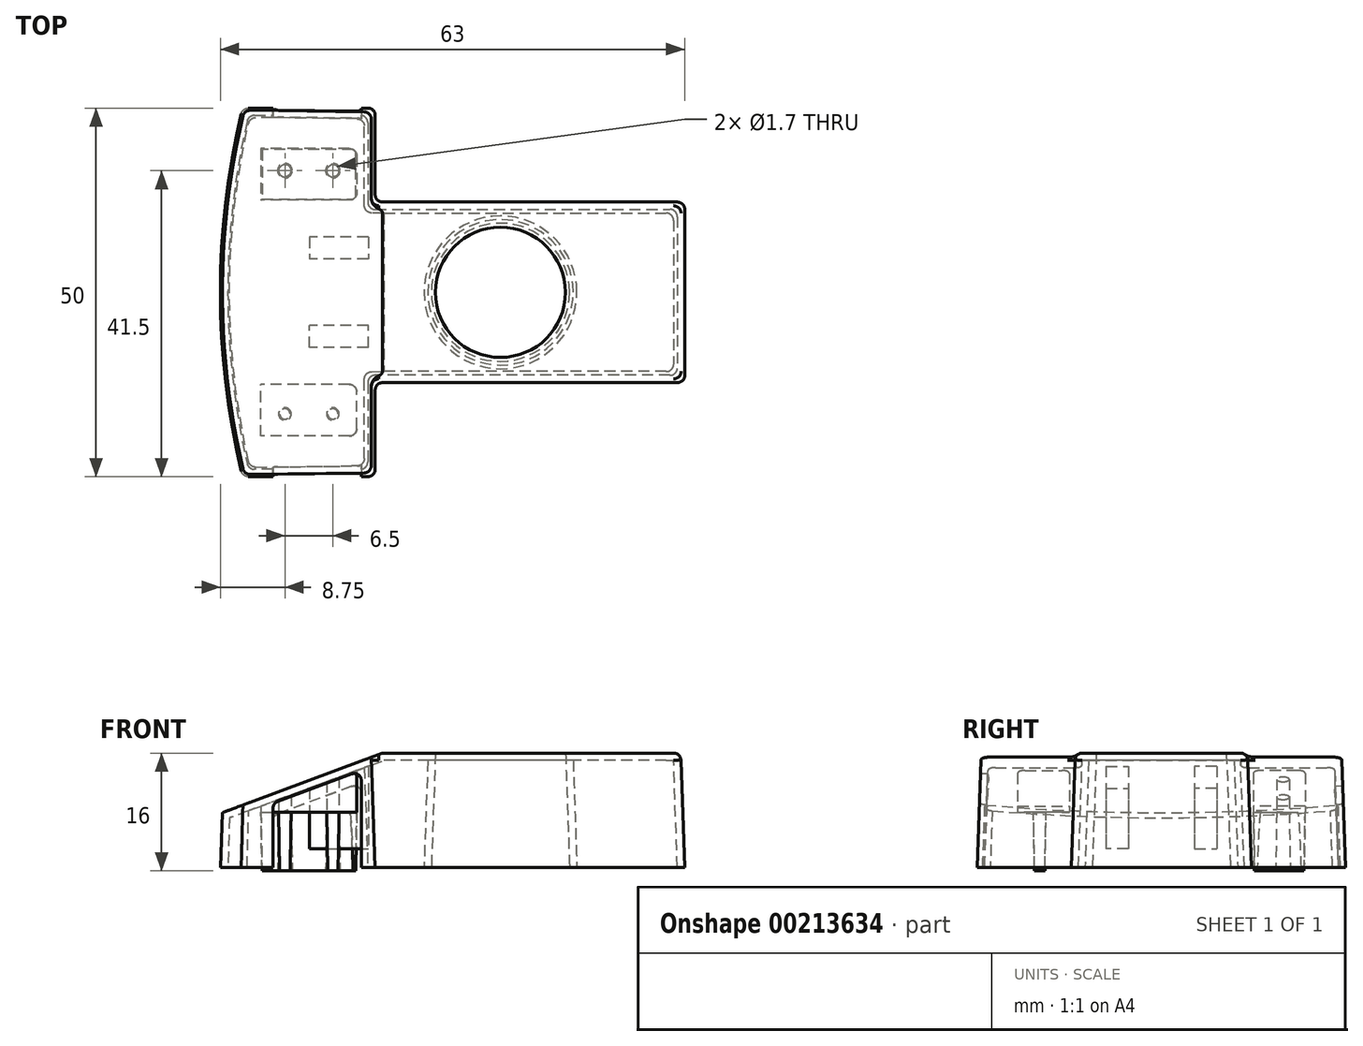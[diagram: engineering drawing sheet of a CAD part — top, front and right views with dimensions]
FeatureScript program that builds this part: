
annotation { "Feature Type Name" : "Feature", "Feature Type Description" : "" }
export const myFeature = defineFeature(function(context is Context, id is Id, definition is map)
    precondition{}
    {
        {
            var Q0;
            Q0=qCreatedBy(makeId("Top.planeOp"),FACE);
            var sketch = newSketch(context, id + "F0", { "sketchPlane" : qUnion([Q0])});
            skCircle(sketch, "E0", {"center": v(-4, 0) * mm, "radius": 9.37 * mm});
            skLineSegment(sketch, "E1.bottom", {"start": v(-21, -12.25) * mm, "end": v(21, -12.25) * mm});
            skLineSegment(sketch, "E1.top", {"start": v(-21, 12.25) * mm, "end": v(21, 12.25) * mm});
            skLineSegment(sketch, "E1.right", {"start": v(21, -12.25) * mm, "end": v(21, 12.25) * mm});
            skLineSegment(sketch, "E2.bottom", {"start": v(-21, -25) * mm, "end": v(-39, -25) * mm});
            skLineSegment(sketch, "E2.top", {"start": v(-21, 25) * mm, "end": v(-39, 25) * mm});
            skLineSegment(sketch, "E2.left", {"start": v(-21, -25) * mm, "end": v(-21, -12.25) * mm});
            skLineSegment(sketch, "E2.right", {"start": v(-39, -25) * mm, "end": v(-39, 25) * mm});
            skPoint(sketch, "E2.middle", {"position": v(-30, 0) * mm});
            skLineSegment(sketch, "E3.trimOffspring", {"start": v(-21, 12.25) * mm, "end": v(-21, 25) * mm});
            skLineSegment(sketch, "E4", {"start": v(-20, 12.25) * mm, "end": v(-20, -12.25) * mm});
            skPoint(sketch, "E5", {"position": v(-42, 0) * mm});
            skPoint(sketch, "E5.positionSnap0", {"position": v(-39, 0) * mm});
            skArc(sketch, "E6", {"start": v(-39, 25) * mm, "mid": v(-42, 0) * mm, "end": v(-39, -25) * mm});
            skSolve(sketch);
        }
        {
            var Q0;
            Q0=qSketchRegion(id+"F0",true);
            var Q1;
            Q1=makeQuery(id+"F0.imprint","IMPRINT",FACE,{"disambiguationData":[TD([[makeQuery(id+"F0.imprint","IMPRINT",EDGE,{"derivedFrom":sQuery(id+"F0.wireOp",EDGE,"E0")}),1.0]])]});
            extrude(context, id + "F1", {"entities" : qUnion([Q0, Q1]), "depth" : 15.5 * mm, "hasDraft" : true, "draftAngle" : 2 * degree, "draftPullDirection" : true});
        }
        {
            var Q0;
            Q0=makeQuery(id+"F0.imprint","IMPRINT",FACE,{"disambiguationData":[TD([[makeQuery(id+"F0.imprint","IMPRINT",EDGE,{"derivedFrom":sQuery(id+"F0.wireOp",EDGE,"E0")}),1.0]])]});
            var Q1;
            Q1=makeQuery(id+"F1.opExtrude","CAP_FACE",FACE,{"disambiguationData":[OSD([sQuery(id+"F0.wireOp",EDGE,"E1.bottom"),sQuery(id+"F0.wireOp",EDGE,"E1.top"),sQuery(id+"F0.wireOp",EDGE,"E1.right"),sQuery(id+"F0.wireOp",EDGE,"E2.bottom"),sQuery(id+"F0.wireOp",EDGE,"E2.top"),sQuery(id+"F0.wireOp",EDGE,"E2.left"),sQuery(id+"F0.wireOp",EDGE,"E3.trimOffspring"),sQuery(id+"F0.wireOp",EDGE,"E6")])],"isStart":false});
            extrude(context, id + "F2", {"entities" : qUnion([Q0]), "operationType" : NewBodyOperationType.REMOVE, "endBound" : BoundingType.UP_TO_SURFACE, "endBoundEntityFace" : qUnion([Q1]), "depth" : 25 * mm, "hasDraft" : true, "draftAngle" : 2 * degree, "draftPullDirection" : true});
        }
        {
            var Q0;
            Q0=qCreatedBy(makeId("Front.planeOp"),FACE);
            var Q1;
            Q1=makeQuery(id+"F1.opExtrude","CAP_EDGE",EDGE,{"disambiguationData":[OSD([sQuery(id+"F0.wireOp",EDGE,"E2.bottom")])],"isStart":true});
            cPlane(context, id + "F3", {"entities" : qUnion([Q0, Q1]), "cplaneType" : CPlaneType.LINE_ANGLE, "offset" : 25 * mm, "angle" : 0 * degree, "width" : 150 * mm, "height" : 150 * mm});
        }
        {
            var Q0;
            Q0=qCreatedBy(id+"F3.planeOp",FACE);
            var sketch = newSketch(context, id + "F4", { "sketchPlane" : qUnion([Q0])});
            skLineSegment(sketch, "E7", {"start": v(20, 15.5) * mm, "end": v(42, 15.5) * mm});
            skLineSegment(sketch, "E8", {"start": v(42, 15.5) * mm, "end": v(42, 7.32) * mm});
            skLineSegment(sketch, "E9", {"start": v(42, 7.32) * mm, "end": v(20, 15.5) * mm});
            skLineSegment(sketch, "E10", {"start": v(42, 0) * mm, "end": v(41.46, 15.5) * mm, "construction": true});
            skLineSegment(sketch, "E11", {"start": v(42, 0) * mm, "end": v(42, 27.73) * mm, "construction": true});
            skSolve(sketch);
        }
        {
            var Q0;
            Q0 = qSketchRegion(id + "F4", true);
            extrude(context, id + "F5", {"entities" : qUnion([Q0]), "operationType" : NewBodyOperationType.REMOVE, "endBound" : BoundingType.THROUGH_ALL, "depth" : 25 * mm});
        }
        {
            var Q0;
            Q0=makeQuery(id+"F1.opExtrude","CAP_FACE",FACE,{"disambiguationData":[OSD([sQuery(id+"F0.wireOp",EDGE,"E1.bottom"),sQuery(id+"F0.wireOp",EDGE,"E1.top"),sQuery(id+"F0.wireOp",EDGE,"E1.right"),sQuery(id+"F0.wireOp",EDGE,"E2.bottom"),sQuery(id+"F0.wireOp",EDGE,"E2.top"),sQuery(id+"F0.wireOp",EDGE,"E2.left"),sQuery(id+"F0.wireOp",EDGE,"E3.trimOffspring"),sQuery(id+"F0.wireOp",EDGE,"E6")])],"isStart":true});
            shell(context, id + "F6", {"entities" : qUnion([Q0]), "thickness" : 1 * mm});
        }
        {
            var Q0;
            Q0=makeQuery(id+"F1.opExtrude","SWEPT_FACE",FACE,{"disambiguationData":[OSD([sQuery(id+"F0.wireOp",EDGE,"E2.bottom")])]});
            var sketch = newSketch(context, id + "F7", { "sketchPlane" : qUnion([Q0])});
            skLineSegment(sketch, "E12", {"start": v(-20, 15.5) * mm, "end": v(-39, 8.43) * mm});
            skLineSegment(sketch, "E13", {"start": v(-39, 8.43) * mm, "end": v(-39, 15.5) * mm});
            skLineSegment(sketch, "E14", {"start": v(-39, 15.5) * mm, "end": v(-20, 15.5) * mm});
            skLineSegment(sketch, "E15", {"start": v(-34.87, -0.87) * mm, "end": v(-34.87, 7.86) * mm});
            skLineSegment(sketch, "E16", {"start": v(-34.87, 7.86) * mm, "end": v(-22.87, 12.32) * mm});
            skLineSegment(sketch, "E17", {"start": v(-22.87, -0.87) * mm, "end": v(-34.87, -0.87) * mm});
            skLineSegment(sketch, "E18", {"start": v(-22.87, 12.32) * mm, "end": v(-22.87, -0.87) * mm});
            skSolve(sketch);
        }
        {
            var Q0;
            Q0=makeQuery(id+"F7.imprint","IMPRINT",FACE,{"disambiguationData":[TD([[makeQuery(id+"F7.imprint","IMPRINT",EDGE,{"derivedFrom":sQuery(id+"F7.wireOp",EDGE,"E15")}),-1.0]])]});
            extrude(context, id + "F8", {"entities" : qUnion([Q0]), "operationType" : NewBodyOperationType.REMOVE, "endBound" : BoundingType.THROUGH_ALL, "oppositeDirection" : true, "depth" : 25 * mm});
        }
        {
            var Q0;
            Q0=makeQuery(id+"F1.opExtrude","CAP_FACE",FACE,{"disambiguationData":[OSD([sQuery(id+"F0.wireOp",EDGE,"E0"),sQuery(id+"F0.wireOp",EDGE,"E1.bottom"),sQuery(id+"F0.wireOp",EDGE,"E1.top"),sQuery(id+"F0.wireOp",EDGE,"E1.right"),sQuery(id+"F0.wireOp",EDGE,"E2.bottom"),sQuery(id+"F0.wireOp",EDGE,"E2.top"),sQuery(id+"F0.wireOp",EDGE,"E2.left"),sQuery(id+"F0.wireOp",EDGE,"E2.right"),sQuery(id+"F0.wireOp",EDGE,"E3.trimOffspring")])],"isStart":false});
            cPlane(context, id + "F9", {"entities" : qUnion([Q0]), "cplaneType" : CPlaneType.OFFSET, "offset" : 8 * mm, "oppositeDirection" : true, "width" : 150 * mm, "height" : 150 * mm});
        }
        {
            var Q0;
            Q0=qCreatedBy(id+"F9.planeOp",FACE);
            var sketch = newSketch(context, id + "F10", { "sketchPlane" : qUnion([Q0])});
            skLineSegment(sketch, "E19", {"start": v(0, 0) * mm, "end": v(-63, 0) * mm, "construction": true});
            skLineSegment(sketch, "E20.bottom", {"start": v(-36.5, -12.5) * mm, "end": v(-23.5, -12.5) * mm});
            skLineSegment(sketch, "E20.top", {"start": v(-36.5, -19.5) * mm, "end": v(-23.5, -19.5) * mm});
            skLineSegment(sketch, "E20.left", {"start": v(-36.5, -12.5) * mm, "end": v(-36.5, -19.5) * mm});
            skLineSegment(sketch, "E20.right", {"start": v(-23.5, -12.5) * mm, "end": v(-23.5, -19.5) * mm});
            skPoint(sketch, "E20.middle", {"position": v(-30, -16) * mm});
            skPoint(sketch, "E21", {"position": v(-33.25, -16.5) * mm});
            skPoint(sketch, "E22", {"position": v(-26.75, -16.5) * mm});
            skCircle(sketch, "E23", {"center": v(-33.25, -16.5) * mm, "radius": 0.85 * mm});
            skCircle(sketch, "E24", {"center": v(-26.75, -16.5) * mm, "radius": 0.85 * mm});
            skLineSegment(sketch, "E25.MirrorCS", {"start": v(-36.5, 12.5) * mm, "end": v(-23.5, 12.5) * mm});
            skLineSegment(sketch, "E26.MirrorCS", {"start": v(-36.5, 12.5) * mm, "end": v(-36.5, 19.5) * mm});
            skLineSegment(sketch, "E27.MirrorCS", {"start": v(-36.5, 19.5) * mm, "end": v(-23.5, 19.5) * mm});
            skLineSegment(sketch, "E28.MirrorCS", {"start": v(-23.5, 12.5) * mm, "end": v(-23.5, 19.5) * mm});
            skCircle(sketch, "E29.MirrorC", {"center": v(-26.75, 16.5) * mm, "radius": 0.85 * mm});
            skCircle(sketch, "E30.MirrorC", {"center": v(-33.25, 16.5) * mm, "radius": 0.85 * mm});
            skSolve(sketch);
        }
        {
            var Q0;
            Q0=makeQuery(id+"F10.imprint","IMPRINT",FACE,{"disambiguationData":[TD([[makeQuery(id+"F10.imprint","IMPRINT",EDGE,{"derivedFrom":sQuery(id+"F10.wireOp",EDGE,"E20.bottom")}),-1.0]])]});
            var Q1;
            Q1=makeQuery(id+"F10.imprint","IMPRINT",FACE,{"disambiguationData":[TD([[makeQuery(id+"F10.imprint","IMPRINT",EDGE,{"derivedFrom":sQuery(id+"F10.wireOp",EDGE,"E23")}),1.0]])]});
            var Q2;
            Q2=makeQuery(id+"F10.imprint","IMPRINT",FACE,{"disambiguationData":[TD([[makeQuery(id+"F10.imprint","IMPRINT",EDGE,{"derivedFrom":sQuery(id+"F10.wireOp",EDGE,"E24")}),1.0]])]});
            var Q3;
            Q3=makeQuery(id+"F10.imprint","IMPRINT",FACE,{"disambiguationData":[TD([[makeQuery(id+"F10.imprint","IMPRINT",EDGE,{"derivedFrom":sQuery(id+"F10.wireOp",EDGE,"E25.MirrorCS")}),1.0]])]});
            var Q4;
            Q4=makeQuery(id+"F10.imprint","IMPRINT",FACE,{"disambiguationData":[TD([[makeQuery(id+"F10.imprint","IMPRINT",EDGE,{"derivedFrom":sQuery(id+"F10.wireOp",EDGE,"E30.MirrorC")}),-1.0]])]});
            var Q5;
            Q5=makeQuery(id+"F10.imprint","IMPRINT",FACE,{"disambiguationData":[TD([[makeQuery(id+"F10.imprint","IMPRINT",EDGE,{"derivedFrom":sQuery(id+"F10.wireOp",EDGE,"E29.MirrorC")}),-1.0]])]});
            var Q6;
            Q6=makeQuery(id+"F6.opShell","OFFSET_FACE",FACE,{"disambiguationData":[OSD([sQuery(id+"F4.wireOp",EDGE,"E9")])]});
            extrude(context, id + "F11", {"entities" : qUnion([Q0, Q1, Q2, Q3, Q4, Q5]), "operationType" : NewBodyOperationType.ADD, "endBound" : BoundingType.UP_TO_SURFACE, "endBoundEntityFace" : qUnion([Q6]), "depth" : 25 * mm});
        }
        {
            var Q0;
            Q0=makeQuery(id+"F10.imprint","IMPRINT",FACE,{"disambiguationData":[TD([[makeQuery(id+"F10.imprint","IMPRINT",EDGE,{"derivedFrom":sQuery(id+"F10.wireOp",EDGE,"E23")}),1.0]])]});
            var Q1;
            Q1=makeQuery(id+"F10.imprint","IMPRINT",FACE,{"disambiguationData":[TD([[makeQuery(id+"F10.imprint","IMPRINT",EDGE,{"derivedFrom":sQuery(id+"F10.wireOp",EDGE,"E29.MirrorC")}),-1.0]])]});
            var Q2;
            Q2=makeQuery(id+"F10.imprint","IMPRINT",FACE,{"disambiguationData":[TD([[makeQuery(id+"F10.imprint","IMPRINT",EDGE,{"derivedFrom":sQuery(id+"F10.wireOp",EDGE,"E30.MirrorC")}),-1.0]])]});
            var Q3;
            Q3=makeQuery(id+"F10.imprint","IMPRINT",FACE,{"disambiguationData":[TD([[makeQuery(id+"F10.imprint","IMPRINT",EDGE,{"derivedFrom":sQuery(id+"F10.wireOp",EDGE,"E24")}),1.0]])]});
            extrude(context, id + "F12", {"entities" : qUnion([Q0, Q1, Q2, Q3]), "operationType" : NewBodyOperationType.ADD, "oppositeDirection" : true, "depth" : 8 * mm, "hasDraft" : true, "draftAngle" : 1 * degree, "draftPullDirection" : true});
        }
        {
            var Q0;
            Q0=makeQuery(id+"F1.opExtrude","CAP_EDGE",EDGE,{"disambiguationData":[OSD([sQuery(id+"F0.wireOp",EDGE,"E1.bottom")])],"isStart":false});
            var Q1;
            Q1=makeQuery(id+"F1.opExtrude","CAP_EDGE",EDGE,{"disambiguationData":[OSD([sQuery(id+"F0.wireOp",EDGE,"E1.right")])],"isStart":false});
            var Q2;
            Q2=makeQuery(id+"F1.opExtrude","CAP_EDGE",EDGE,{"disambiguationData":[OSD([sQuery(id+"F0.wireOp",EDGE,"E1.top")])],"isStart":false});
            var Q3;
            Q3=makeQuery(id+"F1.opExtrude","SWEPT_EDGE",EDGE,{"disambiguationData":[OSD([sQuery(id+"F0.wireOp",EDGE,"E1.bottom"),sQuery(id+"F0.wireOp",EDGE,"E1.right")])]});
            var Q4;
            Q4=makeQuery(id+"F1.opExtrude","SWEPT_EDGE",EDGE,{"disambiguationData":[OSD([sQuery(id+"F0.wireOp",EDGE,"E1.top"),sQuery(id+"F0.wireOp",EDGE,"E1.right")])]});
            fillet(context, id + "F13", {"entities" : qUnion([Q0, Q1, Q2, Q3, Q4]), "radius" : 1 * mm, "tangentPropagation" : true, "allowEdgeOverflow" : false});
        }
        {
            var Q0;
            Q0=makeQuery(id+"F1.opExtrude","SWEPT_EDGE",EDGE,{"disambiguationData":[OSD([sQuery(id+"F0.wireOp",EDGE,"E2.bottom"),sQuery(id+"F0.wireOp",EDGE,"E2.left")])]});
            var Q1;
            Q1=makeQuery(id+"F5.boolean.opBoolean","INTERSECT",EDGE,{"derivedFrom":[makeQuery(id+"F1.opExtrude","SWEPT_FACE",FACE,{"disambiguationData":[OSD([sQuery(id+"F0.wireOp",EDGE,"E2.left")])]}),makeQuery(id+"F5.opExtrude","SWEPT_FACE",FACE,{"disambiguationData":[OSD([sQuery(id+"FjstzwEYRuGCUyq_1.wireOp",EDGE,"6156deb2-2619-4c56-9df6-34b3699534c4")])]})]});
            var Q2;
            Q2=makeQuery(id+"F5.boolean.opBoolean","COPY",EDGE,{"derivedFrom":makeQuery(id+"F5.opExtrude","CAP_EDGE",EDGE,{"disambiguationData":[OSD([sQuery(id+"FjstzwEYRuGCUyq_1.wireOp",EDGE,"6156deb2-2619-4c56-9df6-34b3699534c4")])],"isStart":true})});
            var Q3;
            Q3=makeQuery(id+"F1.opExtrude","SWEPT_EDGE",EDGE,{"disambiguationData":[OSD([sQuery(id+"F0.wireOp",EDGE,"E2.bottom"),sQuery(id+"F0.wireOp",EDGE,"E2.right"),sQuery(id+"F0.wireOp",EDGE,"E6")])]});
            var Q4;
            Q4=makeQuery(id+"F5.boolean.opBoolean","INTERSECT",EDGE,{"derivedFrom":[makeQuery(id+"F1.opExtrude","SWEPT_FACE",FACE,{"disambiguationData":[OSD([sQuery(id+"F0.wireOp",EDGE,"E6")])]}),makeQuery(id+"F5.opExtrude","SWEPT_FACE",FACE,{"disambiguationData":[OSD([sQuery(id+"FjstzwEYRuGCUyq_1.wireOp",EDGE,"6156deb2-2619-4c56-9df6-34b3699534c4")])]})]});
            var Q5;
            Q5=makeQuery(id+"F5.boolean.opBoolean","INTERSECT",EDGE,{"derivedFrom":[makeQuery(id+"F1.opExtrude","SWEPT_FACE",FACE,{"disambiguationData":[OSD([sQuery(id+"F0.wireOp",EDGE,"E2.top")])]}),makeQuery(id+"F5.opExtrude","SWEPT_FACE",FACE,{"disambiguationData":[OSD([sQuery(id+"FjstzwEYRuGCUyq_1.wireOp",EDGE,"6156deb2-2619-4c56-9df6-34b3699534c4")])]})]});
            var Q6;
            Q6=makeQuery(id+"F1.opExtrude","SWEPT_EDGE",EDGE,{"disambiguationData":[OSD([sQuery(id+"F0.wireOp",EDGE,"E2.top"),sQuery(id+"F0.wireOp",EDGE,"E2.right"),sQuery(id+"F0.wireOp",EDGE,"E6")])]});
            var Q7;
            Q7=makeQuery(id+"F1.opExtrude","SWEPT_EDGE",EDGE,{"disambiguationData":[OSD([sQuery(id+"F0.wireOp",EDGE,"E2.top"),sQuery(id+"F0.wireOp",EDGE,"E3.trimOffspring")])]});
            var Q8;
            Q8=makeQuery(id+"F5.boolean.opBoolean","INTERSECT",EDGE,{"derivedFrom":[makeQuery(id+"F1.opExtrude","SWEPT_FACE",FACE,{"disambiguationData":[OSD([sQuery(id+"F0.wireOp",EDGE,"E3.trimOffspring")])]}),makeQuery(id+"F5.opExtrude","SWEPT_FACE",FACE,{"disambiguationData":[OSD([sQuery(id+"FjstzwEYRuGCUyq_1.wireOp",EDGE,"6156deb2-2619-4c56-9df6-34b3699534c4")])]})]});
            fillet(context, id + "F14", {"entities" : qUnion([Q0, Q1, Q2, Q3, Q4, Q5, Q6, Q7, Q8]), "radius" : 1 * mm, "tangentPropagation" : true, "allowEdgeOverflow" : false});
        }
        {
            var Q0;
            Q0=makeQuery(id+"F1.opExtrude","SWEPT_EDGE",EDGE,{"disambiguationData":[OSD([sQuery(id+"F0.wireOp",EDGE,"E1.top"),sQuery(id+"F0.wireOp",EDGE,"E3.trimOffspring")])]});
            fillet(context, id + "F15", {"entities" : qUnion([Q0]), "radius" : 1 * mm, "tangentPropagation" : true, "allowEdgeOverflow" : false});
        }
        {
            var Q0;
            Q0=makeQuery(id+"F1.opExtrude","SWEPT_EDGE",EDGE,{"disambiguationData":[OSD([sQuery(id+"F0.wireOp",EDGE,"E1.bottom"),sQuery(id+"F0.wireOp",EDGE,"E2.left")])]});
            var Q1;
            {var subQ0=sQuery(id+"F0.wireOp",EDGE,"E2.bottom");var subQ1=sQuery(id+"F7.wireOp",EDGE,"E18");Q1=makeQuery(id+"F8.boolean.opBoolean","COPY",EDGE,{"disambiguationData":[TD([makeQuery(id+"F1.opExtrude","SWEPT_FACE",FACE,{"disambiguationData":[OSD([subQ0])]})])],"derivedFrom":makeQuery(id+"F8.opExtrude","SWEPT_EDGE",EDGE,{"disambiguationData":[OSD([subQ0,sQuery(id+"F7.wireOp",EDGE,"E17"),subQ1])]})});}
            var Q2;
            {var subQ0=sQuery(id+"F0.wireOp",EDGE,"E2.bottom");var subQ1=sQuery(id+"F7.wireOp",EDGE,"E15");Q2=makeQuery(id+"F8.boolean.opBoolean","COPY",EDGE,{"disambiguationData":[TD([makeQuery(id+"F1.opExtrude","SWEPT_FACE",FACE,{"disambiguationData":[OSD([subQ0])]})])],"derivedFrom":makeQuery(id+"F8.opExtrude","SWEPT_EDGE",EDGE,{"disambiguationData":[OSD([subQ0,subQ1,sQuery(id+"F7.wireOp",EDGE,"E17")])]})});}
            var Q3;
            {var subQ0=sQuery(id+"F0.wireOp",EDGE,"E2.top");var subQ1=sQuery(id+"F0.wireOp",EDGE,"E2.bottom");var subQ2=sQuery(id+"F7.wireOp",EDGE,"E15");Q3=makeQuery(id+"F8.boolean.opBoolean","COPY",EDGE,{"disambiguationData":[TD([makeQuery(id+"F1.opExtrude","SWEPT_FACE",FACE,{"disambiguationData":[OSD([subQ0])]})])],"derivedFrom":makeQuery(id+"F8.opExtrude","SWEPT_EDGE",EDGE,{"disambiguationData":[OSD([subQ1,subQ2,sQuery(id+"F7.wireOp",EDGE,"E17")])]})});}
            var Q4;
            {var subQ0=sQuery(id+"F0.wireOp",EDGE,"E2.top");var subQ1=sQuery(id+"F0.wireOp",EDGE,"E2.bottom");var subQ2=sQuery(id+"F7.wireOp",EDGE,"E18");Q4=makeQuery(id+"F8.boolean.opBoolean","COPY",EDGE,{"disambiguationData":[TD([makeQuery(id+"F1.opExtrude","SWEPT_FACE",FACE,{"disambiguationData":[OSD([subQ0])]})])],"derivedFrom":makeQuery(id+"F8.opExtrude","SWEPT_EDGE",EDGE,{"disambiguationData":[OSD([subQ1,sQuery(id+"F7.wireOp",EDGE,"E17"),subQ2])]})});}
            var Q5;
            {var subQ0=sQuery(id+"F0.wireOp",EDGE,"E2.top");var subQ1=sQuery(id+"F7.wireOp",EDGE,"E18");var subQ2=sQuery(id+"F7.wireOp",EDGE,"E16");Q5=makeQuery(id+"F8.boolean.opBoolean","COPY",EDGE,{"disambiguationData":[TD([makeQuery(id+"F1.opExtrude","SWEPT_FACE",FACE,{"disambiguationData":[OSD([subQ0])]})])],"derivedFrom":makeQuery(id+"F8.opExtrude","SWEPT_EDGE",EDGE,{"disambiguationData":[OSD([subQ2,subQ1])]})});}
            var Q6;
            {var subQ0=sQuery(id+"F0.wireOp",EDGE,"E2.top");var subQ1=sQuery(id+"F7.wireOp",EDGE,"E15");var subQ2=sQuery(id+"F7.wireOp",EDGE,"E16");Q6=makeQuery(id+"F8.boolean.opBoolean","COPY",EDGE,{"disambiguationData":[TD([makeQuery(id+"F1.opExtrude","SWEPT_FACE",FACE,{"disambiguationData":[OSD([subQ0])]})])],"derivedFrom":makeQuery(id+"F8.opExtrude","SWEPT_EDGE",EDGE,{"disambiguationData":[OSD([subQ1,subQ2])]})});}
            var Q7;
            {var subQ0=sQuery(id+"F0.wireOp",EDGE,"E2.bottom");var subQ1=sQuery(id+"F7.wireOp",EDGE,"E18");var subQ2=sQuery(id+"F7.wireOp",EDGE,"E16");Q7=makeQuery(id+"F8.boolean.opBoolean","COPY",EDGE,{"disambiguationData":[TD([makeQuery(id+"F1.opExtrude","SWEPT_FACE",FACE,{"disambiguationData":[OSD([subQ0])]})])],"derivedFrom":makeQuery(id+"F8.opExtrude","SWEPT_EDGE",EDGE,{"disambiguationData":[OSD([subQ2,subQ1])]})});}
            var Q8;
            {var subQ0=sQuery(id+"F0.wireOp",EDGE,"E2.bottom");var subQ1=sQuery(id+"F7.wireOp",EDGE,"E15");var subQ2=sQuery(id+"F7.wireOp",EDGE,"E16");Q8=makeQuery(id+"F8.boolean.opBoolean","COPY",EDGE,{"disambiguationData":[TD([makeQuery(id+"F1.opExtrude","SWEPT_FACE",FACE,{"disambiguationData":[OSD([subQ0])]})])],"derivedFrom":makeQuery(id+"F8.opExtrude","SWEPT_EDGE",EDGE,{"disambiguationData":[OSD([subQ1,subQ2])]})});}
            var Q9;
            Q9=makeQuery(id+"F6.opShell","OFFSET_EDGE",EDGE,{"disambiguationData":[OSD([sQuery(id+"F0.wireOp",EDGE,"E1.top"),sQuery(id+"F0.wireOp",EDGE,"E3.trimOffspring")])]});
            var Q10;
            Q10=makeQuery(id+"F6.opShell","OFFSET_EDGE",EDGE,{"disambiguationData":[OSD([sQuery(id+"F0.wireOp",EDGE,"E1.bottom"),sQuery(id+"F0.wireOp",EDGE,"E2.left")])]});
            fillet(context, id + "F16", {"entities" : qUnion([Q0, Q1, Q2, Q3, Q4, Q5, Q6, Q7, Q8, Q9, Q10]), "radius" : 1 * mm, "tangentPropagation" : true, "allowEdgeOverflow" : false});
        }
        {
            var Q0;
            Q0=makeQuery(id+"F6.opShell","OFFSET_EDGE",EDGE,{"disambiguationData":[OSD([sQuery(id+"F0.wireOp",EDGE,"E1.top"),sQuery(id+"F0.wireOp",EDGE,"E1.right")])]});
            var Q1;
            Q1=makeQuery(id+"F6.opShell","OFFSET_EDGE",EDGE,{"disambiguationData":[OSD([sQuery(id+"F0.wireOp",EDGE,"E1.bottom"),sQuery(id+"F0.wireOp",EDGE,"E1.right")])]});
            var Q2;
            {var subQ0=sQuery(id+"F0.wireOp",EDGE,"E0");Q2=makeQuery(id+"F6.opShell","OFFSET_EDGE",EDGE,{"disambiguationData":[OSD([subQ0]),TDD([makeQuery(id+"F1.opExtrude","CAP_EDGE",EDGE,{"disambiguationData":[OSD([subQ0])],"isStart":false})])]});}
            var Q3;
            Q3=makeQuery(id+"F6.opShell","OFFSET_EDGE",EDGE,{"disambiguationData":[OSD([sQuery(id+"F0.wireOp",EDGE,"E2.top"),sQuery(id+"F0.wireOp",EDGE,"E3.trimOffspring")])]});
            var Q4;
            Q4=makeQuery(id+"F6.opShell","OFFSET_EDGE",EDGE,{"disambiguationData":[OSD([sQuery(id+"F0.wireOp",EDGE,"E2.top"),sQuery(id+"F0.wireOp",EDGE,"E2.right"),sQuery(id+"F0.wireOp",EDGE,"E6")])]});
            var Q5;
            Q5=makeQuery(id+"F6.opShell","OFFSET_EDGE",EDGE,{"disambiguationData":[OSD([sQuery(id+"F0.wireOp",EDGE,"E2.bottom"),sQuery(id+"F0.wireOp",EDGE,"E2.left")])]});
            var Q6;
            Q6=makeQuery(id+"F6.opShell","OFFSET_EDGE",EDGE,{"disambiguationData":[OSD([sQuery(id+"F0.wireOp",EDGE,"E2.bottom"),sQuery(id+"F0.wireOp",EDGE,"E2.right"),sQuery(id+"F0.wireOp",EDGE,"E6")])]});
            var Q7;
            Q7=makeQuery(id+"F11.opExtrude","SWEPT_EDGE",EDGE,{"disambiguationData":[OSD([sQuery(id+"F10.wireOp",EDGE,"E20.bottom"),sQuery(id+"F10.wireOp",EDGE,"E20.right")])]});
            var Q8;
            Q8=makeQuery(id+"F11.opExtrude","SWEPT_EDGE",EDGE,{"disambiguationData":[OSD([sQuery(id+"F10.wireOp",EDGE,"E20.top"),sQuery(id+"F10.wireOp",EDGE,"E20.right")])]});
            var Q9;
            Q9=makeQuery(id+"F11.opExtrude","SWEPT_EDGE",EDGE,{"disambiguationData":[OSD([sQuery(id+"F10.wireOp",EDGE,"E27.MirrorCS"),sQuery(id+"F10.wireOp",EDGE,"E28.MirrorCS")])]});
            var Q10;
            Q10=makeQuery(id+"F11.opExtrude","SWEPT_EDGE",EDGE,{"disambiguationData":[OSD([sQuery(id+"F10.wireOp",EDGE,"E25.MirrorCS"),sQuery(id+"F10.wireOp",EDGE,"E28.MirrorCS")])]});
            fillet(context, id + "F17", {"entities" : qUnion([Q0, Q1, Q2, Q3, Q4, Q5, Q6, Q7, Q8, Q9, Q10]), "radius" : 1 * mm, "tangentPropagation" : true, "allowEdgeOverflow" : false});
        }
        {
            var Q0;
            Q0=qCreatedBy(id+"F9.planeOp",FACE);
            var sketch = newSketch(context, id + "F18", { "sketchPlane" : qUnion([Q0])});
            skPoint(sketch, "E31", {"position": v(-29.94, -4.5) * mm});
            skLineSegment(sketch, "E32.bottom", {"start": v(-29.94, -4.5) * mm, "end": v(-21.94, -4.5) * mm});
            skLineSegment(sketch, "E32.top", {"start": v(-29.94, -7.5) * mm, "end": v(-21.94, -7.5) * mm});
            skLineSegment(sketch, "E32.left", {"start": v(-29.94, -4.5) * mm, "end": v(-29.94, -7.5) * mm});
            skLineSegment(sketch, "E32.right", {"start": v(-21.94, -4.5) * mm, "end": v(-21.94, -7.5) * mm});
            skLineSegment(sketch, "E33", {"start": v(0, 0) * mm, "end": v(-48.4, 0) * mm, "construction": true});
            skLineSegment(sketch, "E34.MirrorCS", {"start": v(-29.94, 4.5) * mm, "end": v(-21.94, 4.5) * mm});
            skLineSegment(sketch, "E35.MirrorCS", {"start": v(-21.94, 4.5) * mm, "end": v(-21.94, 7.5) * mm});
            skLineSegment(sketch, "E36.MirrorCS", {"start": v(-29.94, 7.5) * mm, "end": v(-21.94, 7.5) * mm});
            skLineSegment(sketch, "E37.MirrorCS", {"start": v(-29.94, 4.5) * mm, "end": v(-29.94, 7.5) * mm});
            skSolve(sketch);
        }
        {
            var Q0;
            Q0=qSketchRegion(id+"F18",true);
            var Q1;
            Q1=makeQuery(id+"F6.opShell","OFFSET_FACE",FACE,{"disambiguationData":[OSD([sQuery(id+"F4.wireOp",EDGE,"E9")])]});
            extrude(context, id + "F19", {"entities" : qUnion([Q0]), "operationType" : NewBodyOperationType.ADD, "endBound" : BoundingType.UP_TO_SURFACE, "endBoundEntityFace" : qUnion([Q1]), "depth" : 25 * mm, "hasSecondDirection" : true, "secondDirectionOppositeDirection" : true, "secondDirectionDepth" : 5 * mm});
        }
    });
